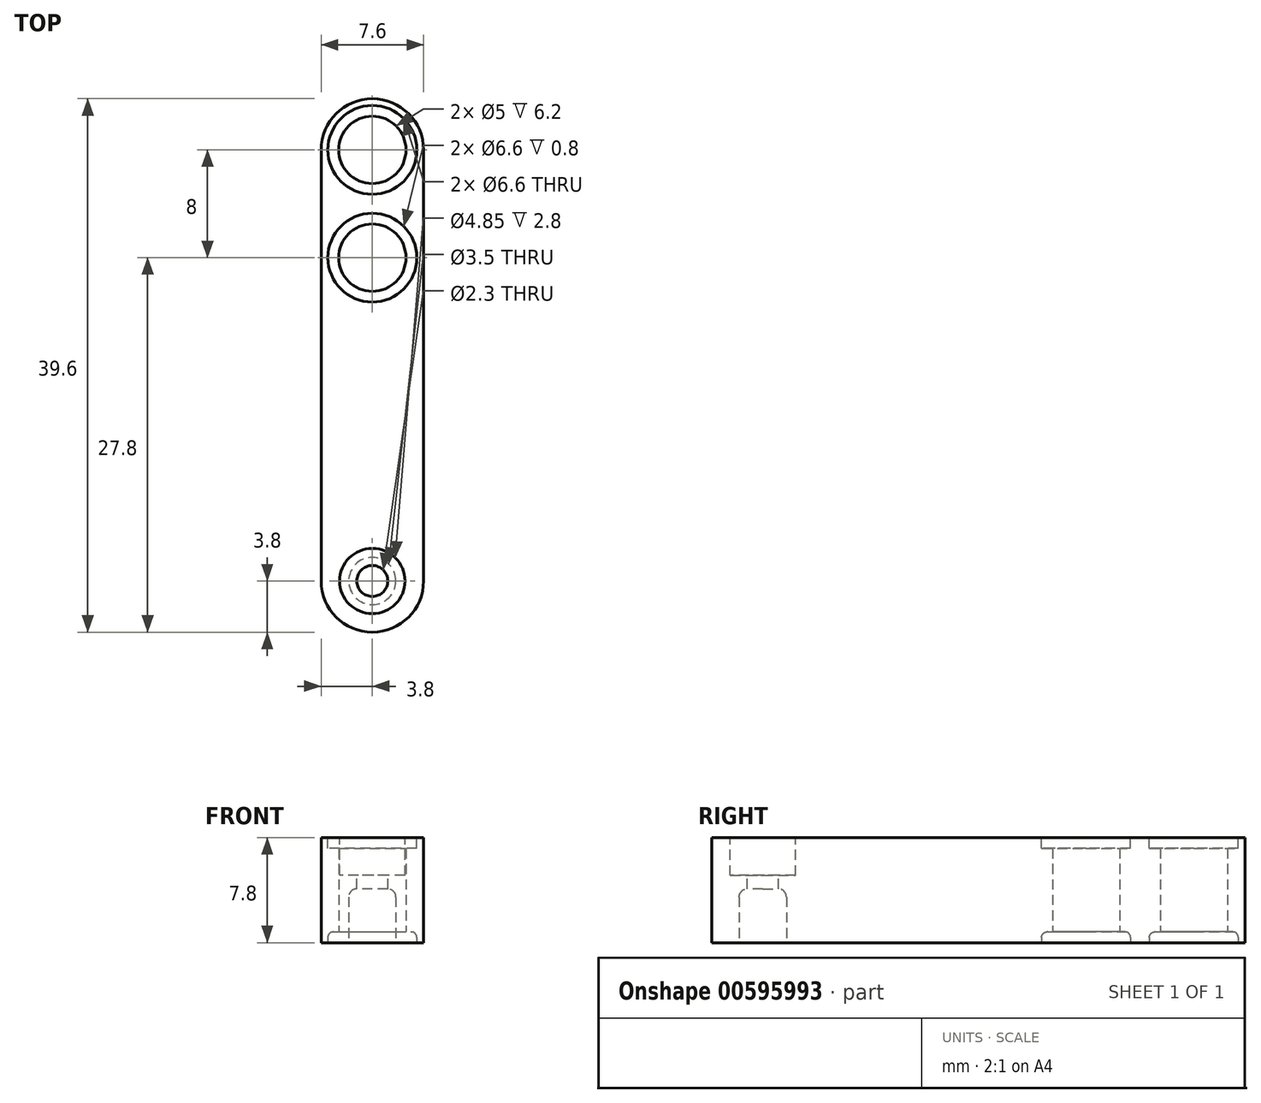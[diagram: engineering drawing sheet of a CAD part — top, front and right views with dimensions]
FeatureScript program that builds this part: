
annotation { "Feature Type Name" : "Feature", "Feature Type Description" : "" }
export const myFeature = defineFeature(function(context is Context, id is Id, definition is map)
    precondition{}
    {
        {
            var Q0;
            Q0=qCreatedBy(makeId("Top.planeOp"),FACE);
            var sketch = newSketch(context, id + "F0", { "sketchPlane" : qUnion([Q0])});
            skLineSegment(sketch, "E0", {"start": v(0, 0) * mm, "end": v(0, 32) * mm});
            skLineSegment(sketch, "E1", {"start": v(7.6, 32) * mm, "end": v(7.6, 0) * mm});
            skArc(sketch, "E2", {"start": v(0, 32) * mm, "mid": v(3.8, 35.8) * mm, "end": v(7.6, 32) * mm});
            skArc(sketch, "E3", {"start": v(7.6, 0) * mm, "mid": v(3.8, -3.8) * mm, "end": v(0, 0) * mm});
            skCircle(sketch, "E4", {"center": v(3.8, 32) * mm, "radius": 2.5 * mm});
            skCircle(sketch, "E5", {"center": v(3.8, 24) * mm, "radius": 2.5 * mm});
            skSolve(sketch);
        }
        {
            var Q0;
            Q0 = qSketchRegion(id + "F0", true);
            extrude(context, id + "F1", {"entities" : qUnion([Q0]), "depth" : 7.8 * mm, "offsetDistance" : 25 * mm});
        }
        {
            var Q0;
            Q0=makeQuery(id+"F1.opExtrude","CAP_FACE",FACE,{"disambiguationData":[OSD([sQuery(id+"F0.wireOp",EDGE,"E0"),sQuery(id+"F0.wireOp",EDGE,"E1"),sQuery(id+"F0.wireOp",EDGE,"E2"),sQuery(id+"F0.wireOp",EDGE,"E3"),sQuery(id+"F0.wireOp",EDGE,"E4"),sQuery(id+"F0.wireOp",EDGE,"E5")])],"isStart":false});
            var sketch = newSketch(context, id + "F2", { "sketchPlane" : qUnion([Q0])});
            skCircle(sketch, "E6.0", {"center": v(3.8, 32) * mm, "radius": 2.5 * mm, "construction": true});
            skCircle(sketch, "E7.0", {"center": v(3.8, 24) * mm, "radius": 2.5 * mm, "construction": true});
            skCircle(sketch, "E8.0", {"center": v(3.8, 32) * mm, "radius": 3.3 * mm});
            skCircle(sketch, "E9.0", {"center": v(3.8, 24) * mm, "radius": 3.3 * mm});
            skSolve(sketch);
        }
        {
            var Q0;
            Q0 = qSketchRegion(id + "F2", true);
            extrude(context, id + "F3", {"entities" : qUnion([Q0]), "operationType" : NewBodyOperationType.REMOVE, "oppositeDirection" : true, "depth" : 0.8 * mm, "offsetDistance" : 25 * mm});
        }
        {
            var Q0;
            Q0=makeQuery(id+"F1.opExtrude","CAP_FACE",FACE,{"disambiguationData":[OSD([sQuery(id+"F0.wireOp",EDGE,"E0"),sQuery(id+"F0.wireOp",EDGE,"E1"),sQuery(id+"F0.wireOp",EDGE,"E2"),sQuery(id+"F0.wireOp",EDGE,"E3"),sQuery(id+"F0.wireOp",EDGE,"E4"),sQuery(id+"F0.wireOp",EDGE,"E5")])],"isStart":true});
            var sketch = newSketch(context, id + "F4", { "sketchPlane" : qUnion([Q0])});
            skCircle(sketch, "E10.0", {"center": v(3.8, -24) * mm, "radius": 3.3 * mm});
            skCircle(sketch, "E11.0", {"center": v(3.8, -32) * mm, "radius": 3.3 * mm});
            skSolve(sketch);
        }
        {
            var Q0;
            Q0 = qSketchRegion(id + "F4", true);
            extrude(context, id + "F5", {"entities" : qUnion([Q0]), "operationType" : NewBodyOperationType.REMOVE, "oppositeDirection" : true, "depth" : 0.8 * mm, "offsetDistance" : 25 * mm});
        }
        {
            var Q0;
            Q0=makeQuery(id+"F1.opExtrude","CAP_FACE",FACE,{"disambiguationData":[OSD([sQuery(id+"F0.wireOp",EDGE,"E0"),sQuery(id+"F0.wireOp",EDGE,"E1"),sQuery(id+"F0.wireOp",EDGE,"E2"),sQuery(id+"F0.wireOp",EDGE,"E3"),sQuery(id+"F0.wireOp",EDGE,"E4"),sQuery(id+"F0.wireOp",EDGE,"E5")])],"isStart":false});
            var sketch = newSketch(context, id + "F6", { "sketchPlane" : qUnion([Q0])});
            skCircle(sketch, "E12", {"center": v(3.8, 0) * mm, "radius": 2.43 * mm});
            skSolve(sketch);
        }
        {
            var Q0;
            Q0 = qSketchRegion(id + "F6", true);
            extrude(context, id + "F7", {"entities" : qUnion([Q0]), "operationType" : NewBodyOperationType.REMOVE, "oppositeDirection" : true, "depth" : 2.8 * mm, "offsetDistance" : 25 * mm});
        }
        {
            var Q0;
            Q0=makeQuery(id+"F1.opExtrude","CAP_FACE",FACE,{"disambiguationData":[OSD([sQuery(id+"F0.wireOp",EDGE,"E0"),sQuery(id+"F0.wireOp",EDGE,"E1"),sQuery(id+"F0.wireOp",EDGE,"E2"),sQuery(id+"F0.wireOp",EDGE,"E3"),sQuery(id+"F0.wireOp",EDGE,"E4"),sQuery(id+"F0.wireOp",EDGE,"E5")])],"isStart":true});
            var sketch = newSketch(context, id + "F8", { "sketchPlane" : qUnion([Q0])});
            skCircle(sketch, "E13", {"center": v(3.8, 0) * mm, "radius": 1.75 * mm});
            skSolve(sketch);
        }
        {
            var Q0;
            Q0 = qSketchRegion(id + "F8", true);
            extrude(context, id + "F9", {"entities" : qUnion([Q0]), "operationType" : NewBodyOperationType.REMOVE, "oppositeDirection" : true, "depth" : 4 * mm, "offsetDistance" : 25 * mm});
        }
        {
            var Q0;
            Q0=makeQuery(id+"F7.boolean.opBoolean","COPY",FACE,{"derivedFrom":makeQuery(id+"F7.opExtrude","CAP_FACE",FACE,{"disambiguationData":[OSD([sQuery(id+"F6.wireOp",EDGE,"E12")])],"isStart":false})});
            var sketch = newSketch(context, id + "F10", { "sketchPlane" : qUnion([Q0])});
            skCircle(sketch, "E14", {"center": v(3.8, 0) * mm, "radius": 1.15 * mm});
            skSolve(sketch);
        }
        {
            var Q0;
            Q0 = qSketchRegion(id + "F10", true);
            extrude(context, id + "F11", {"entities" : qUnion([Q0]), "operationType" : NewBodyOperationType.REMOVE, "endBound" : BoundingType.THROUGH_ALL, "oppositeDirection" : true, "depth" : 25 * mm, "offsetDistance" : 25 * mm});
        }
        {
            var Q0;
            Q0=makeQuery(id+"F9.boolean.opBoolean","COPY",EDGE,{"derivedFrom":makeQuery(id+"F9.opExtrude","CAP_EDGE",EDGE,{"disambiguationData":[OSD([sQuery(id+"F8.wireOp",EDGE,"E13")])],"isStart":false})});
            fillet(context, id + "F12", {"entities" : qUnion([Q0]), "radius" : 0.6 * mm, "tangentPropagation" : true, "allowEdgeOverflow" : false});
        }
        {
            var Q0;
            Q0=makeQuery(id+"F5.boolean.opBoolean","COPY",EDGE,{"derivedFrom":makeQuery(id+"F5.opExtrude","CAP_EDGE",EDGE,{"disambiguationData":[OSD([sQuery(id+"F4.wireOp",EDGE,"E10.0")])],"isStart":false})});
            var Q1;
            Q1=makeQuery(id+"F5.boolean.opBoolean","COPY",EDGE,{"derivedFrom":makeQuery(id+"F5.opExtrude","CAP_EDGE",EDGE,{"disambiguationData":[OSD([sQuery(id+"F4.wireOp",EDGE,"E11.0")])],"isStart":false})});
            fillet(context, id + "F13", {"entities" : qUnion([Q0, Q1]), "radius" : 0.4 * mm, "tangentPropagation" : true, "allowEdgeOverflow" : false});
        }
    });
